# Revit family: WRKN160MF
name_source: partatom
category: Furniture
revit_build: Autodesk Revit 2017 (Build: 20160225_1515(x64)
units: mm (PartAtom-declared; Revit-internal decimal feet)

## family parameters
Always vertical = Yes
Cut with Voids When Loaded = No
Room Calculation Point = No
Shared = No
Work Plane-Based = No

## types (1)
- WRKN160MF
    Adjustability = Seat height, seat depth, multi postion back lock, tension adjustment, back recline of 22°, multi-adjustable arms, fully adjustable headrest
    AssetType = Moveable
    BIMObjectName = NBS_Senator_OfficeChairs_i-Workchair_WRKN160MF
    Category = Pr_40_50_12_57:Office chairs
    CodePerformance = ANSI/BIFMA X5.1-2011, BS EN 1335
    ComponentFinishOptions = Black
    Depth = 460 mm  [stored 1.50919 ft]
    Description = Task chair with black components, 4D arms and headrest
    DurationUnit = year
    ExpectedLife = 10
    FootHeight = 70 mm  [stored 0.229659 ft]
    FrameColourOptions = Black
    FrameMountingMaterial = NBS_Concept
    Has4DArms = No
    HasAnthraciteComponents = No
    HasHeadrest = Yes
    HasPolishedComponents = No
    HighestSeatingHeight = 565 mm
    IfcExportAs = IfcFurnitureType
    IfcExportType = CHAIR
    IsBuiltIn = No
    LegHeight = 377 mm  [stored 1.23688 ft]
    LowestSeatingHeight = 440 mm
    ManufacturerName = Senator
    ManufacturerURL = www.senator.co.uk
    ModelNumber = WRKN160MF
    ModelReference = i-Workchair
    NBSCertification = www.nationalbimlibrary.com/cert/tldw0ekz
    NBSDescription = Office chairs
    NBSReference = 45-35-20/330
    Name = OfficeChairs_i-Workchair_WRKN160MF_Senator
    NominalDepth = 660 mm
    NominalHeight = 1285 mm
    NominalLength = 760 mm
    OfficeChairBase = NBS_Senator_OffcChrs_i-Workchair_5StarBase
    OfficeChairMechanism = NBS_Senator_OffcChrs_i-Workchair_TiltMechanism
    OfficeChairSeat = NBS_Senator_OffcChrs_i-Workchair_Seat
    ProductInformation = www.thesenatorgroup.com<userpath>/_iworkchair.pdf
    SeatArmFrameMaterial = NBS_Concept
    SeatArmMaterial = NBS_Concept
    SeatBaseMaterial = NBS_Concept
    SeatFrameMaterial = NBS_Concept
    SeatTiltMaterial = NBS_Concept
    SeatingHeight = 502 mm  [stored 1.64698 ft]
    SeatingSeatBackMaterial = NBS_Concept
    SeatingSeatMaterial = NBS_Concept
    SeatsAndBacksColourOptions = Onyx,Zinc,Stone,Berry,Forest,Blue,Oyster White
    Size = 760 x 660 x 1285 mm
    StandardsDimensions = ANSI/BIFMA X5.1-2011, BSEN 1335-1 2000
    StandardsDurability = ANSI/BIFMA X5.1-2011, BSEN 1335-3 2009
    StandardsSafetyRequirements = ANSI/BIFMA X5.1-2011, BSEN 1335-2 2009
    Status = UNSET
    SustainabilityPerformance = 100% recycleable
    Uniclass2015Code = Pr_40_50_12_57
    Uniclass2015Title = Office chairs
    Uniclass2015Version = Products v1.9
    Version = 1
    WarrantyDescription = Senator warrants that its manufactured products are free from defects for a period of ten years on Senator seating ranges
    WarrantyDurationParts = 10
    WarrantyDurationUnit = year
    Width = 524 mm  [stored 1.71916 ft]

note: [stored X ft] marks values corroborated as IEEE doubles in the binary element streams (Revit-internal decimal feet)

## geometry (parser evidence)
native form markers: Sweep x10
no freeform markers — native parametric forms only
